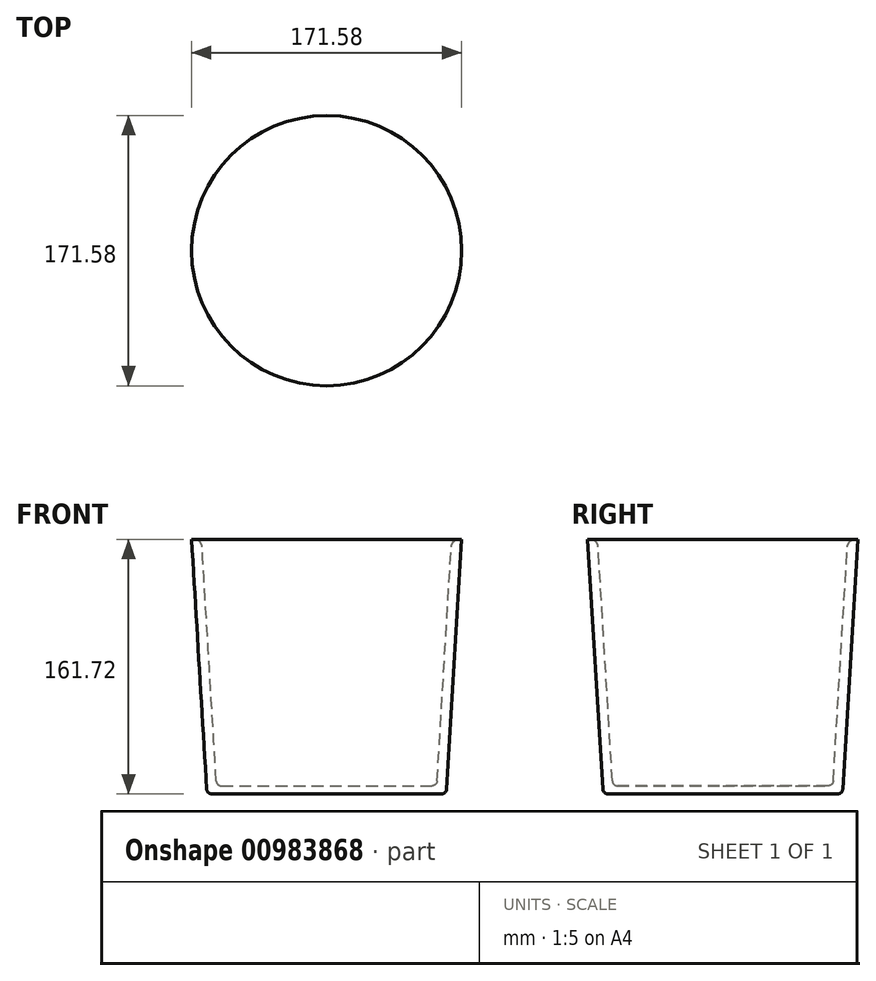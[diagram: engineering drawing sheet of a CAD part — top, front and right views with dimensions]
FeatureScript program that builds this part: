
annotation { "Feature Type Name" : "Feature", "Feature Type Description" : "" }
export const myFeature = defineFeature(function(context is Context, id is Id, definition is map)
    precondition{}
    {
        {
            var Q0;
            Q0=qCreatedBy(makeId("Right.planeOp"),FACE);
            var sketch = newSketch(context, id + "F0", { "sketchPlane" : qUnion([Q0])});
            skLineSegment(sketch, "E0", {"start": v(0, 0) * mm, "end": v(-73.03, 0) * mm});
            skLineSegment(sketch, "E1", {"start": v(-76.2, 2.98) * mm, "end": v(-85.79, 161.72) * mm});
            skLineSegment(sketch, "E2", {"start": v(-85.79, 161.72) * mm, "end": v(-84.21, 161.72) * mm});
            skLineSegment(sketch, "E3", {"start": v(-79.14, 156.94) * mm, "end": v(-70.14, 8.1) * mm});
            skLineSegment(sketch, "E4", {"start": v(-66.97, 5.12) * mm, "end": v(0, 5.12) * mm});
            skPoint(sketch, "E5.visualSharp", {"position": v(-76.01, 0) * mm});
            skArc(sketch, "E5.filletArc", {"start": v(-76.2, 2.98) * mm, "mid": v(-75.2, 0.86) * mm, "end": v(-73.03, 0) * mm});
            skPoint(sketch, "E6.visualSharp", {"position": v(-69.96, 5.12) * mm});
            skArc(sketch, "E6.filletArc", {"start": v(-70.14, 8.1) * mm, "mid": v(-69.15, 5.99) * mm, "end": v(-66.97, 5.12) * mm});
            skPoint(sketch, "E7.visualSharp", {"position": v(-79.43, 161.72) * mm});
            skArc(sketch, "E7.filletArc", {"start": v(-79.14, 156.94) * mm, "mid": v(-80.73, 160.33) * mm, "end": v(-84.21, 161.72) * mm});
            skLineSegment(sketch, "E8", {"start": v(0, 0) * mm, "end": v(0, 5.12) * mm});
            skSolve(sketch);
        }
        {
            var Q0;
            Q0=makeQuery(id+"F0.imprint","IMPRINT",FACE,{"disambiguationData":[TD([[makeQuery(id+"F0.imprint","IMPRINT",EDGE,{"derivedFrom":sQuery(id+"F0.wireOp",EDGE,"E0")}),-1.0]])]});
            var Q1;
            Q1=sQuery(id+"F0.wireOp",EDGE,"E8");
            revolve(context, id + "F1", {"surfaceOperationType" : NewSurfaceOperationType.NEW, "entities" : qUnion([Q0]), "axis" : qUnion([Q1]), "revolveType" : RevolveType.FULL});
        }
    });
